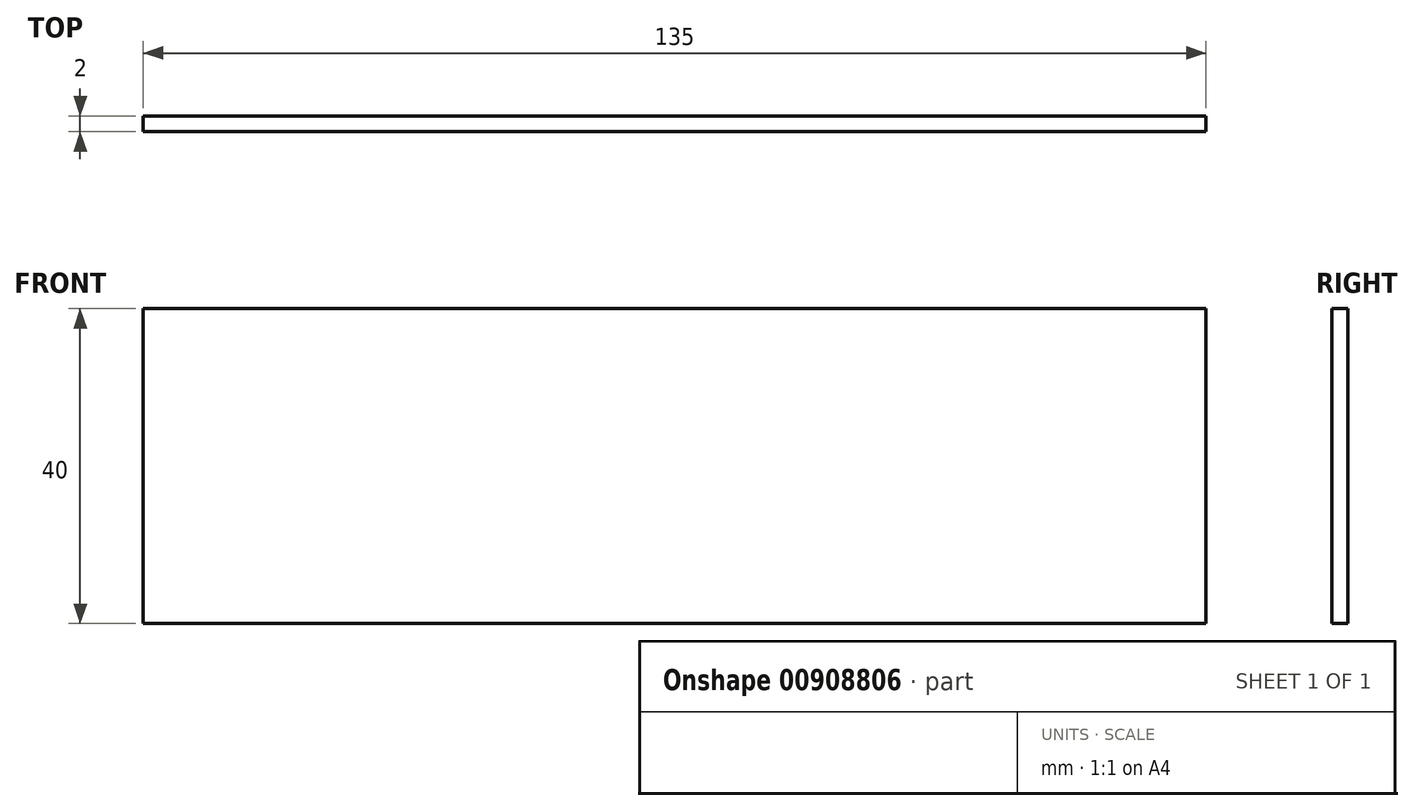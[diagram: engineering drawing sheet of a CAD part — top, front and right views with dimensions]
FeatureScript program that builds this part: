
annotation { "Feature Type Name" : "Feature", "Feature Type Description" : "" }
export const myFeature = defineFeature(function(context is Context, id is Id, definition is map)
    precondition{}
    {
        {
            var Q0;
            Q0=qCreatedBy(makeId("Front.planeOp"),FACE);
            var sketch = newSketch(context, id + "F0", { "sketchPlane" : qUnion([Q0])});
            skLineSegment(sketch, "E0.bottom", {"start": v(67.5, -20) * mm, "end": v(-67.5, -20) * mm});
            skLineSegment(sketch, "E0.top", {"start": v(67.5, 20) * mm, "end": v(-67.5, 20) * mm});
            skLineSegment(sketch, "E0.left", {"start": v(67.5, -20) * mm, "end": v(67.5, 20) * mm});
            skLineSegment(sketch, "E0.right", {"start": v(-67.5, -20) * mm, "end": v(-67.5, 20) * mm});
            skPoint(sketch, "E0.middle", {"position": v(0, 0) * mm});
            skSolve(sketch);
        }
        {
            var Q0;
            Q0=qSketchRegion(id+"F0",true);
            extrude(context, id + "F1", {"entities" : qUnion([Q0]), "depth" : 2 * mm});
        }
    });
